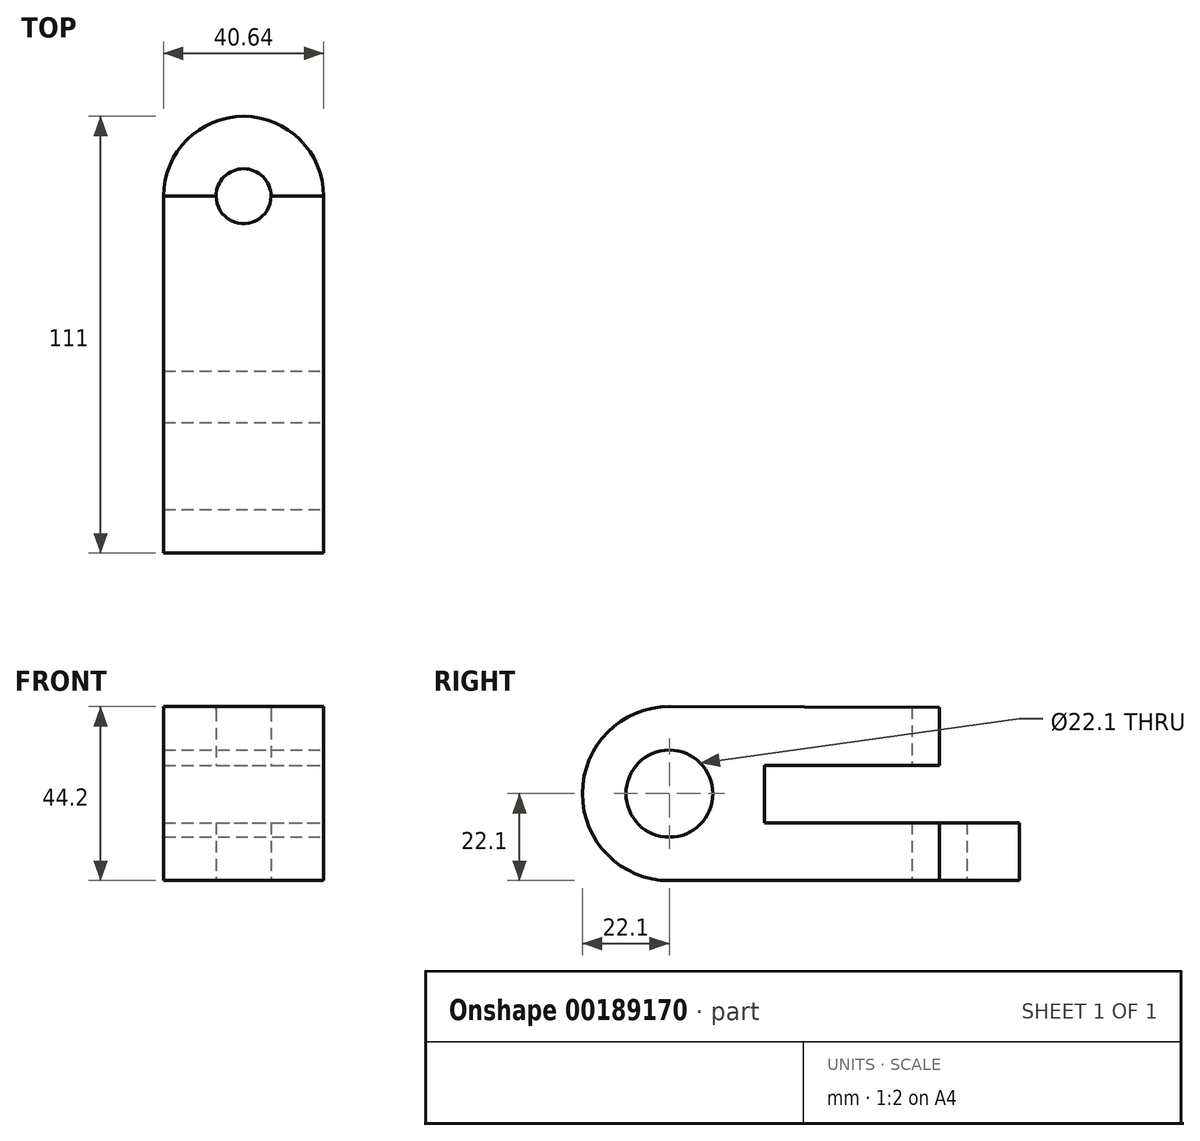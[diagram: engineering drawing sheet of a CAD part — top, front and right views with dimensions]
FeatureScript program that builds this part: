
annotation { "Feature Type Name" : "Feature", "Feature Type Description" : "" }
export const myFeature = defineFeature(function(context is Context, id is Id, definition is map)
    precondition{}
    {
        {
            var Q0;
            Q0=qCreatedBy(makeId("Right.planeOp"),FACE);
            var sketch = newSketch(context, id + "F0", { "sketchPlane" : qUnion([Q0])});
            skArc(sketch, "E0", {"start": v(0, 22.1) * mm, "mid": v(-22.1, 0) * mm, "end": v(0, -22.1) * mm});
            skArc(sketch, "E1", {"start": v(0, 22.1) * mm, "mid": v(-22.15, 0) * mm, "end": v(0, -22.1) * mm});
            skLineSegment(sketch, "E2", {"start": v(0, 22.1) * mm, "end": v(68.58, 21.94) * mm});
            skLineSegment(sketch, "E3", {"start": v(68.58, 21.94) * mm, "end": v(68.58, 7.2) * mm});
            skLineSegment(sketch, "E4", {"start": v(68.58, 7.2) * mm, "end": v(24.13, 7.2) * mm});
            skLineSegment(sketch, "E5", {"start": v(24.13, 7.2) * mm, "end": v(24.13, -7.37) * mm});
            skLineSegment(sketch, "E6", {"start": v(24.13, -7.37) * mm, "end": v(68.58, -7.37) * mm});
            skLineSegment(sketch, "E7", {"start": v(0, -22.1) * mm, "end": v(68.58, -22.1) * mm});
            skLineSegment(sketch, "E8", {"start": v(68.58, -22.1) * mm, "end": v(68.58, -7.37) * mm});
            skSolve(sketch);
        }
        {
            var Q0;
            Q0=makeQuery(id+"F0.imprint","IMPRINT",FACE,{"disambiguationData":[TD([[makeQuery(id+"F0.imprint","IMPRINT",EDGE,{"derivedFrom":sQuery(id+"F0.wireOp",EDGE,"E0")}),1.0]])]});
            extrude(context, id + "F1", {"entities" : qUnion([Q0]), "oppositeDirection" : true, "depth" : 40.64 * mm});
        }
        {
            var Q0;
            Q0=qCreatedBy(makeId("Right.planeOp"),FACE);
            var sketch = newSketch(context, id + "F2", { "sketchPlane" : qUnion([Q0])});
            skPoint(sketch, "E9", {"position": v(0, 0) * mm});
            skSolve(sketch);
        }
        {
            var Q0;
            Q0=sQuery(id+"F2.wireOp",VERTEX,"E9");
            var Q1;
            Q1=makeQuery(id+"F1.opExtrude","SWEPT_BODY",BODY,{"disambiguationData":[OSD([sQuery(id+"F0.wireOp",EDGE,"E0"),sQuery(id+"F0.wireOp",EDGE,"E2"),sQuery(id+"F0.wireOp",EDGE,"E3"),sQuery(id+"F0.wireOp",EDGE,"E4"),sQuery(id+"F0.wireOp",EDGE,"E5"),sQuery(id+"F0.wireOp",EDGE,"E6"),sQuery(id+"F0.wireOp",EDGE,"E7"),sQuery(id+"F0.wireOp",EDGE,"E8")])]});
            hole(context, id + "F3", {"style" : HoleStyle.SIMPLE, "endStyle" : HoleEndStyle.THROUGH, "holeDiameter" : 22.1 * mm, "locations" : qUnion([Q0]), "scope" : qUnion([Q1]), "isTappedThrough" : true});
        }
        {
            var Q0;
            Q0=makeQuery(id+"F1.opExtrude","SWEPT_FACE",FACE,{"disambiguationData":[OSD([sQuery(id+"F0.wireOp",EDGE,"E2")])]});
            var sketch = newSketch(context, id + "F4", { "sketchPlane" : qUnion([Q0])});
            skLineSegment(sketch, "E10.0.0", {"start": v(0, -0.05) * mm, "end": v(0, 68.53) * mm});
            skLineSegment(sketch, "E10.0.1", {"start": v(0, 68.53) * mm, "end": v(-40.64, 68.53) * mm});
            skLineSegment(sketch, "E10.0.2", {"start": v(-40.64, 68.53) * mm, "end": v(-40.64, -0.05) * mm});
            skLineSegment(sketch, "E10.0.3", {"start": v(-40.64, -0.05) * mm, "end": v(0, -0.05) * mm});
            skArc(sketch, "E11", {"start": v(0, 68.53) * mm, "mid": v(-20.32, 88.85) * mm, "end": v(-40.64, 68.53) * mm});
            skSolve(sketch);
        }
        {
            var Q0;
            Q0=makeQuery(id+"F4.imprint","IMPRINT",FACE,{"disambiguationData":[TD([[makeQuery(id+"F4.imprint","IMPRINT",EDGE,{"derivedFrom":sQuery(id+"F4.wireOp",EDGE,"E10.0.1")}),1.0]])]});
            extrude(context, id + "F5", {"entities" : qUnion([Q0]), "operationType" : NewBodyOperationType.ADD, "oppositeDirection" : true, "depth" : 14.73 * mm});
        }
        {
            var Q0;
            Q0=makeQuery(id+"F1.opExtrude","SWEPT_FACE",FACE,{"disambiguationData":[OSD([sQuery(id+"F0.wireOp",EDGE,"E7")])]});
            var sketch = newSketch(context, id + "F6", { "sketchPlane" : qUnion([Q0])});
            skLineSegment(sketch, "E12.0.0", {"start": v(0, -68.58) * mm, "end": v(0, 0) * mm});
            skLineSegment(sketch, "E12.0.1", {"start": v(0, 0) * mm, "end": v(-40.64, 0) * mm});
            skLineSegment(sketch, "E12.0.2", {"start": v(-40.64, 0) * mm, "end": v(-40.64, -68.58) * mm});
            skLineSegment(sketch, "E12.0.3", {"start": v(-40.64, -68.58) * mm, "end": v(0, -68.58) * mm});
            skArc(sketch, "E13", {"start": v(-40.64, -68.58) * mm, "mid": v(-20.32, -88.9) * mm, "end": v(0, -68.58) * mm});
            skSolve(sketch);
        }
        {
            var Q0;
            Q0=makeQuery(id+"F6.imprint","IMPRINT",FACE,{"disambiguationData":[TD([[makeQuery(id+"F6.imprint","IMPRINT",EDGE,{"derivedFrom":sQuery(id+"F6.wireOp",EDGE,"E12.0.3")}),-1.0]])]});
            extrude(context, id + "F7", {"entities" : qUnion([Q0]), "oppositeDirection" : true, "depth" : 14.73 * mm});
        }
        {
            var Q0;
            Q0=makeQuery(id+"F1.opExtrude","SWEPT_FACE",FACE,{"disambiguationData":[OSD([sQuery(id+"F0.wireOp",EDGE,"E7")])]});
            var sketch = newSketch(context, id + "F8", { "sketchPlane" : qUnion([Q0])});
            skPoint(sketch, "E14", {"position": v(-20.32, -68.58) * mm});
            skSolve(sketch);
        }
        {
            var Q0;
            Q0=sQuery(id+"F8.wireOp",VERTEX,"E14");
            var Q1;
            Q1=makeQuery(id+"F1.opExtrude","SWEPT_BODY",BODY,{"disambiguationData":[OSD([sQuery(id+"F0.wireOp",EDGE,"E0"),sQuery(id+"F0.wireOp",EDGE,"E2"),sQuery(id+"F0.wireOp",EDGE,"E3"),sQuery(id+"F0.wireOp",EDGE,"E4"),sQuery(id+"F0.wireOp",EDGE,"E5"),sQuery(id+"F0.wireOp",EDGE,"E6"),sQuery(id+"F0.wireOp",EDGE,"E7"),sQuery(id+"F0.wireOp",EDGE,"E8")])]});
            var Q2;
            Q2=makeQuery(id+"F7.opExtrude","SWEPT_BODY",BODY,{"disambiguationData":[OSD([sQuery(id+"F6.wireOp",EDGE,"E12.0.3"),sQuery(id+"F6.wireOp",EDGE,"E13")])]});
            hole(context, id + "F9", {"style" : HoleStyle.SIMPLE, "endStyle" : HoleEndStyle.THROUGH, "holeDiameter" : 13.97 * mm, "locations" : qUnion([Q0]), "scope" : qUnion([Q1, Q2]), "isTappedThrough" : true});
        }
    });
